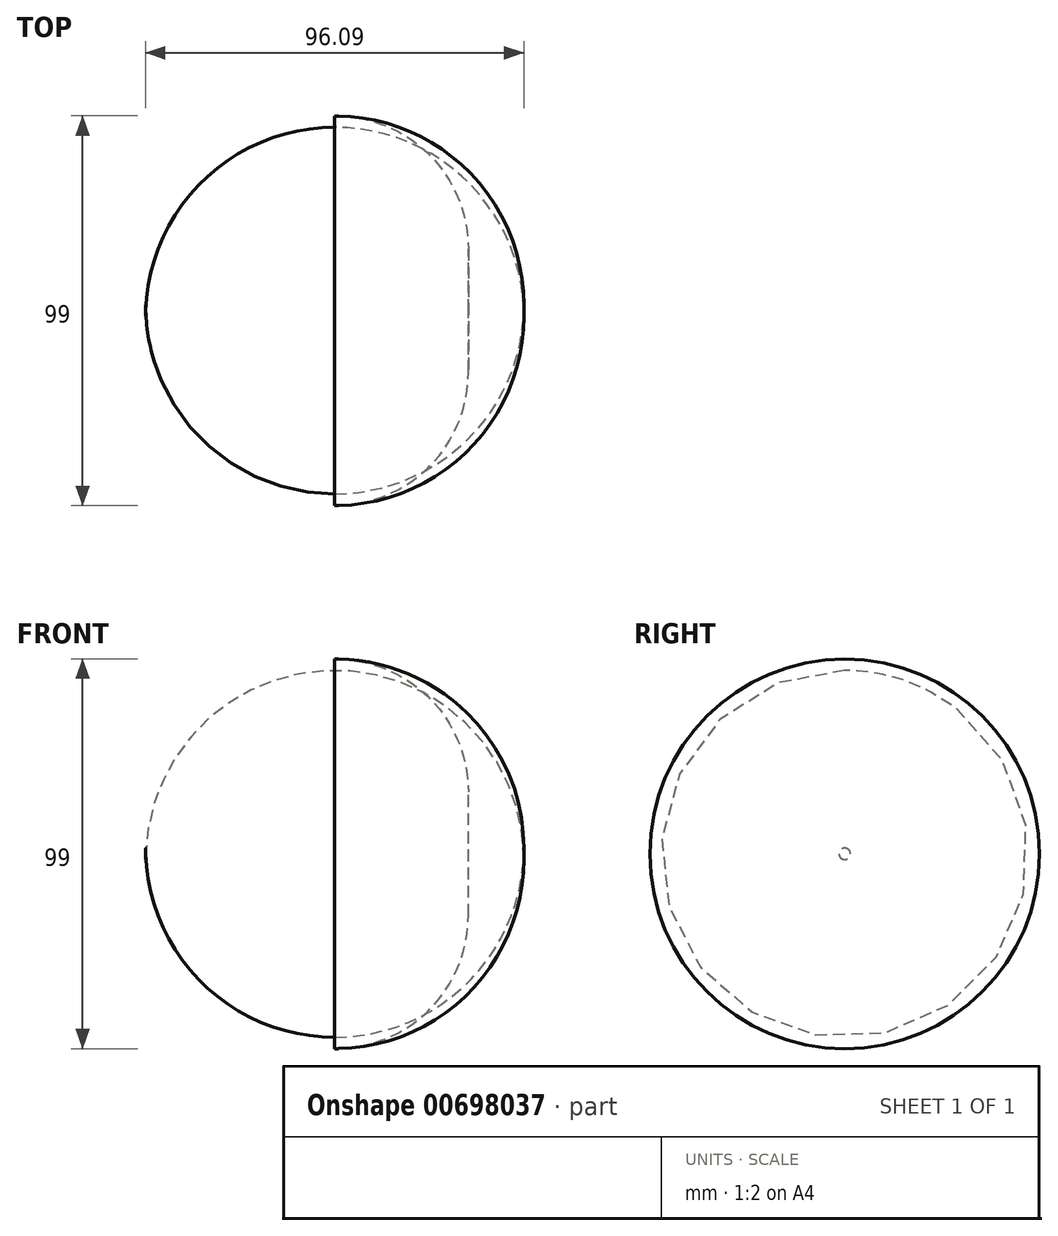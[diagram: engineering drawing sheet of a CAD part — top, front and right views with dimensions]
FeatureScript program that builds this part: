
annotation { "Feature Type Name" : "Feature", "Feature Type Description" : "" }
export const myFeature = defineFeature(function(context is Context, id is Id, definition is map)
    precondition{}
    {
        {
            var Q0;
            Q0=qCreatedBy(makeId("Right.planeOp"),FACE);
            var sketch = newSketch(context, id + "F0", { "sketchPlane" : qUnion([Q0])});
            skCircle(sketch, "E0", {"center": v(0, 0) * mm, "radius": 49.5 * mm});
            skSolve(sketch);
        }
        {
            var Q0;
            Q0 = qSketchRegion(id + "F0", true);
            extrude(context, id + "F1", {"entities" : qUnion([Q0]), "oppositeDirection" : true, "depth" : 41 * mm, "offsetDistance" : 25 * mm, "hasSecondDirection" : true, "secondDirectionOppositeDirection" : false, "secondDirectionDepth" : 41 * mm});
        }
        {
            var Q0;
            Q0=makeQuery(id+"F1.opExtrude","CAP_EDGE",EDGE,{"disambiguationData":[OSD([sQuery(id+"F0.wireOp",EDGE,"E0")])],"isStart":false});
            fillet(context, id + "F2", {"entities" : qUnion([Q0]), "radius" : 48.04 * mm, "tangentPropagation" : true, "allowEdgeOverflow" : false});
        }
        {
            var Q0;
            Q0=makeQuery(id+"F1.opExtrude","CAP_EDGE",EDGE,{"disambiguationData":[OSD([sQuery(id+"F0.wireOp",EDGE,"E0")])],"isStart":true});
            fillet(context, id + "F3", {"entities" : qUnion([Q0]), "radius" : 33.8 * mm, "tangentPropagation" : true, "allowEdgeOverflow" : false});
        }
    });
